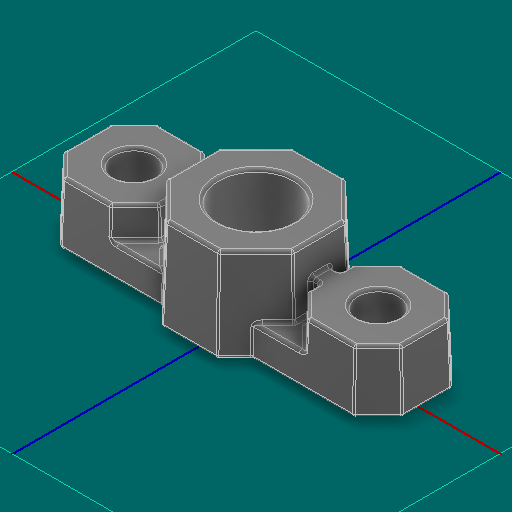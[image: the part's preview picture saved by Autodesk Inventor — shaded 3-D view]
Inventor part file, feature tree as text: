
AUTODESK INVENTOR PART (.ipt)
format: ipt  version: 2025 (Build 290162000, 162)  size: 829,440 bytes
history: native  units: in
note: dims shown in document units (in); Inventor stores cm internally (conversion verified against a paired STEP export)
features: other x8, fillet x2
ambient origin geometry x8: Origin, YZ Plane, XZ Plane, XY Plane, X Axis, Y Axis, Z Axis, Center Point
bodies: Body1 (feature_tree)
feature tree (10):
  other  "HS Bearing Flat.ipt"
  fillet  "Fillet7::HS Bearing Flat.ipt"  Radius=0.3937in
  other  "TaggingFeature1"
  fillet  "Fillet7"  [1 undecoded]
  other  "iInsert:6"
  other  "iInsert:3"
  other  "iInsert:5"
  other  "iInsert:1"
  other  "iInsert:2"
  other  "iInsert:4"
note: 1 required parameter value undecoded (feature->parameter linkage not recoverable at this tier; creation-order binding heuristic only, values carry confidence <= 0.55)
